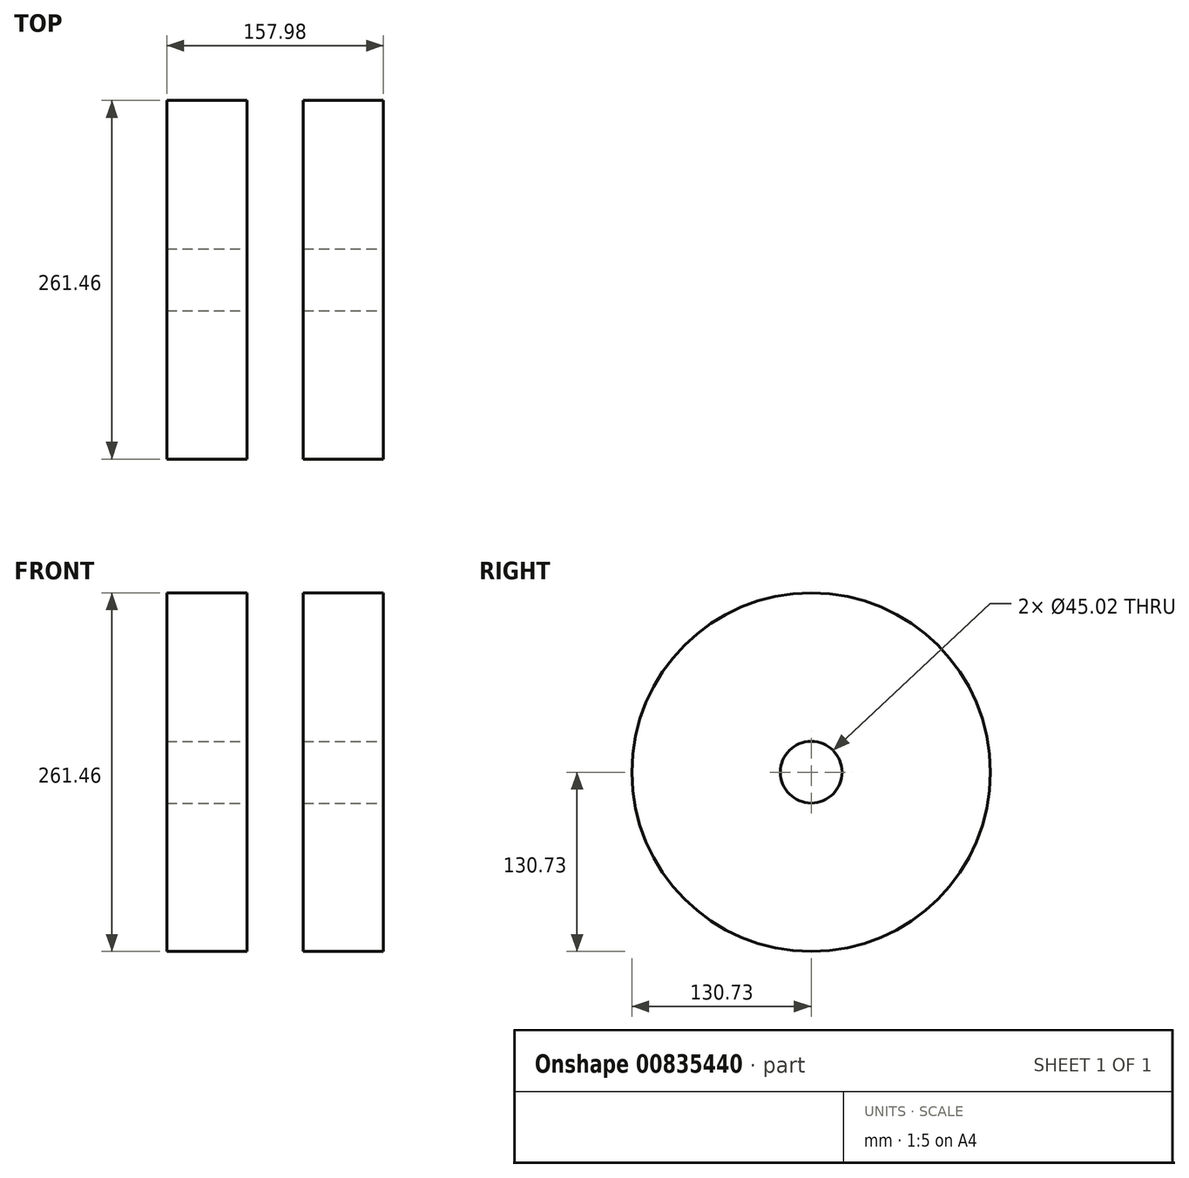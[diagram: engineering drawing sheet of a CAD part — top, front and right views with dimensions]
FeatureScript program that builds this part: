
annotation { "Feature Type Name" : "Feature", "Feature Type Description" : "" }
export const myFeature = defineFeature(function(context is Context, id is Id, definition is map)
    precondition{}
    {
        {
            var Q0;
            Q0=qCreatedBy(makeId("Front.planeOp"),FACE);
            var sketch = newSketch(context, id + "F0", { "sketchPlane" : qUnion([Q0])});
            skLineSegment(sketch, "E0", {"start": v(0, 130.73) * mm, "end": v(0, 0) * mm, "construction": true});
            skLineSegment(sketch, "E1.bottom", {"start": v(-79, 130.73) * mm, "end": v(-20.55, 130.73) * mm});
            skLineSegment(sketch, "E1.top", {"start": v(-79, 22.51) * mm, "end": v(-20.55, 22.51) * mm});
            skLineSegment(sketch, "E1.left", {"start": v(-79, 130.73) * mm, "end": v(-79, 22.51) * mm});
            skLineSegment(sketch, "E1.right", {"start": v(-20.55, 130.73) * mm, "end": v(-20.55, 22.51) * mm});
            skLineSegment(sketch, "E2.MirrorCS", {"start": v(20.55, 130.73) * mm, "end": v(20.55, 22.51) * mm});
            skLineSegment(sketch, "E3.MirrorCS", {"start": v(79, 22.51) * mm, "end": v(20.55, 22.51) * mm});
            skLineSegment(sketch, "E4.MirrorCS", {"start": v(79, 130.73) * mm, "end": v(20.55, 130.73) * mm});
            skLineSegment(sketch, "E5.MirrorCS", {"start": v(79, 130.73) * mm, "end": v(79, 22.51) * mm});
            skSolve(sketch);
        }
        {
            var Q0;
            Q0 = qSketchRegion(id + "F0", true);
            var sketch = newSketch(context, id + "F1", { "sketchPlane" : qUnion([Q0])});
            skLineSegment(sketch, "E6", {"start": v(-84.37, 0) * mm, "end": v(83.15, 0) * mm, "construction": true});
            skSolve(sketch);
        }
        {
            var Q0;
            Q0=sQuery(id+"F0.wireOp",EDGE,"E1.top");
            var Q1;
            Q1=sQuery(id+"F0.wireOp",EDGE,"E1.right");
            var Q2;
            Q2=sQuery(id+"F0.wireOp",EDGE,"E1.left");
            var Q3;
            Q3=sQuery(id+"F0.wireOp",EDGE,"E1.bottom");
            var Q4;
            Q4=sQuery(id+"F0.wireOp",EDGE,"E4.MirrorCS");
            var Q5;
            Q5=sQuery(id+"F0.wireOp",EDGE,"E5.MirrorCS");
            var Q6;
            Q6=sQuery(id+"F0.wireOp",EDGE,"E2.MirrorCS");
            var Q7;
            Q7=sQuery(id+"F0.wireOp",EDGE,"E3.MirrorCS");
            var Q8;
            Q8=sQuery(id+"F1.wireOp",EDGE,"E6");
            revolve(context, id + "F2", {"bodyType" : ToolBodyType.SURFACE, "surfaceOperationType" : NewSurfaceOperationType.NEW, "surfaceEntities" : qUnion([Q0, Q1, Q2, Q3, Q4, Q5, Q6, Q7]), "axis" : qUnion([Q8]), "revolveType" : RevolveType.FULL});
        }
    });
